# Revit family: Cullen Pendant
name_source: partatom
category: Lighting Fixtures
revit_build: Autodesk Revit 2017 (Build: 20190508_0315(x64)
units: mm (PartAtom-declared; Revit-internal decimal feet)

## family parameters
Cut with Voids When Loaded = No
Host = Face
Light Source = Yes
Part Type = Normal
Room Calculation Point = No
Round Connector Dimension = Use Diameter
Shared = No

## types (1)
- Cullen Pendant
    Canopy Width = 5"
    Color Filter = 16777215
    Cost = 179 $
    Default Elevation = 0"
    Description = The Cullen Pendant is what a fixture looks like when stripped down to the simplest expressions of color, light, and form. Ideally suited for experimenting with our wide selection of decorative and energy-saving light bulbs. Assembled in our Portland, Ore. factory using ethically-sourced domestic and global components. A Schoolhouse Original.
    Dimming Lamp Color Temperature Shift = <None>
    Height = 10"
    Light Source Symbol Size = 2"
    Max Wattage = 60 W
    Primary Finishes = Natural Black, White, Persimmon, Black
    Product Material = Steel
    URL = https://www.schoolhouse.com
    Voltage = 120 /220V
    Width = 2"

## geometry (parser evidence)
native form markers: Sweep x3
no freeform markers — native parametric forms only
